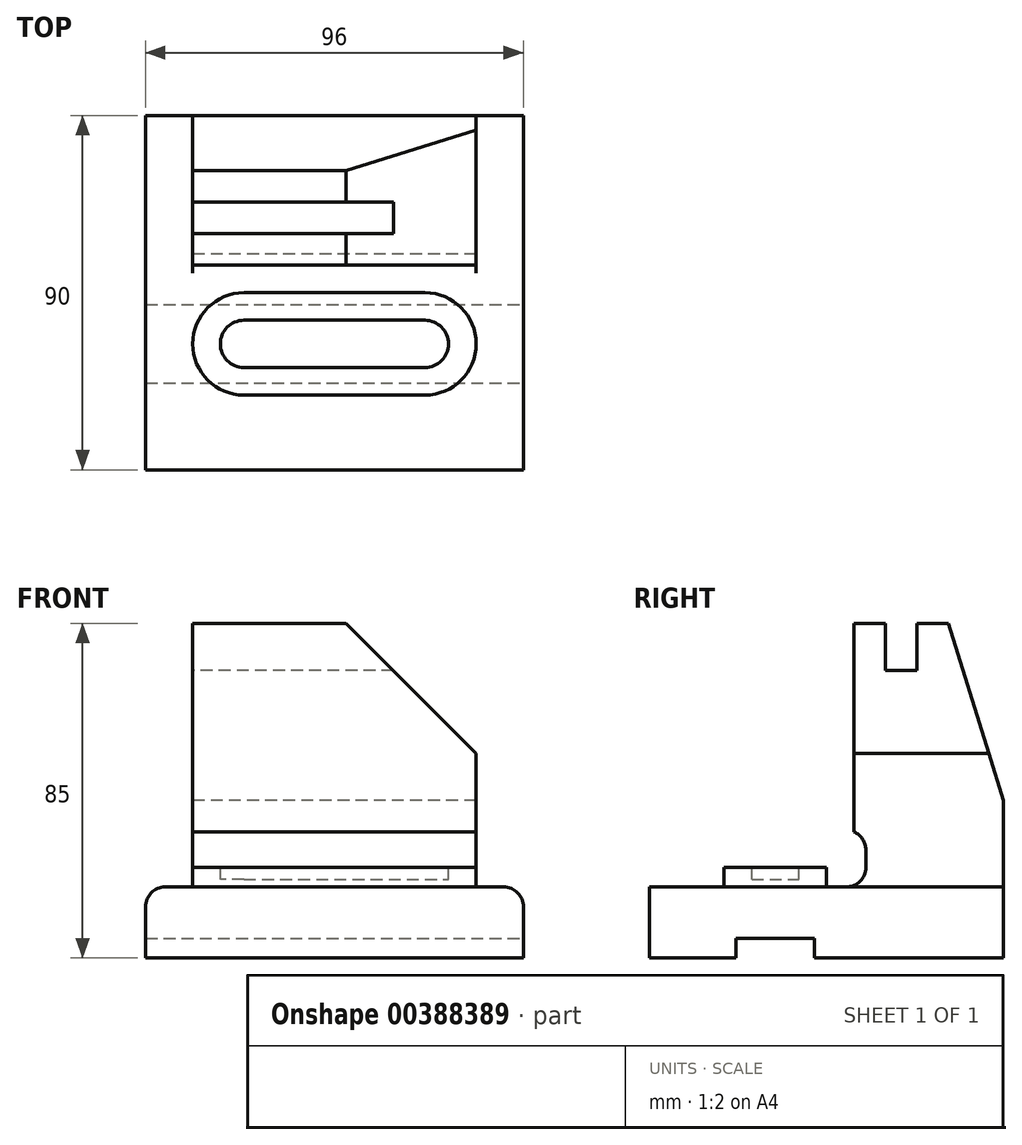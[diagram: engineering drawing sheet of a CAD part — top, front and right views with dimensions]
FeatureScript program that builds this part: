
annotation { "Feature Type Name" : "Feature", "Feature Type Description" : "" }
export const myFeature = defineFeature(function(context is Context, id is Id, definition is map)
    precondition{}
    {
        {
            var Q0;
            Q0=qCreatedBy(makeId("Top.planeOp"),FACE);
            var sketch = newSketch(context, id + "F0", { "sketchPlane" : qUnion([Q0])});
            skLineSegment(sketch, "E0.bottom", {"start": v(0, 0) * mm, "end": v(96, 0) * mm});
            skLineSegment(sketch, "E0.top", {"start": v(0, 90) * mm, "end": v(96, 90) * mm});
            skLineSegment(sketch, "E0.left", {"start": v(0, 0) * mm, "end": v(0, 90) * mm});
            skLineSegment(sketch, "E0.right", {"start": v(96, 0) * mm, "end": v(96, 90) * mm});
            skSolve(sketch);
        }
        {
            var Q0;
            Q0=makeQuery(id+"F0.imprint","IMPRINT",FACE,{"disambiguationData":[TD([[makeQuery(id+"F0.imprint","IMPRINT",EDGE,{"derivedFrom":sQuery(id+"F0.wireOp",EDGE,"E0.bottom")}),1.0]])]});
            extrude(context, id + "F1", {"entities" : qUnion([Q0]), "depth" : 18 * mm});
        }
        {
            var Q0;
            Q0=makeQuery(id+"F1.opExtrude","CAP_FACE",FACE,{"disambiguationData":[OSD([sQuery(id+"F0.wireOp",EDGE,"E0.bottom"),sQuery(id+"F0.wireOp",EDGE,"E0.top"),sQuery(id+"F0.wireOp",EDGE,"E0.left"),sQuery(id+"F0.wireOp",EDGE,"E0.right")])],"isStart":false});
            var sketch = newSketch(context, id + "F2", { "sketchPlane" : qUnion([Q0])});
            skLineSegment(sketch, "E1.bottom", {"start": v(12, 90) * mm, "end": v(84, 90) * mm});
            skLineSegment(sketch, "E1.top", {"start": v(12, 52) * mm, "end": v(84, 52) * mm});
            skLineSegment(sketch, "E1.left", {"start": v(12, 90) * mm, "end": v(12, 52) * mm});
            skLineSegment(sketch, "E1.right", {"start": v(84, 90) * mm, "end": v(84, 52) * mm});
            skSolve(sketch);
        }
        {
            var Q0;
            Q0=makeQuery(id+"F1.opExtrude","CAP_FACE",FACE,{"disambiguationData":[OSD([sQuery(id+"F0.wireOp",EDGE,"E0.bottom"),sQuery(id+"F0.wireOp",EDGE,"E0.top"),sQuery(id+"F0.wireOp",EDGE,"E0.left"),sQuery(id+"F0.wireOp",EDGE,"E0.right")])],"isStart":true});
            cPlane(context, id + "F3", {"entities" : qUnion([Q0]), "cplaneType" : CPlaneType.OFFSET, "offset" : 85 * mm, "oppositeDirection" : true, "width" : 150 * mm, "height" : 150 * mm});
        }
        {
            var Q0;
            Q0 = qSketchRegion(id + "F2", true);
            var Q1;
            Q1=qCreatedBy(id+"F3.planeOp",FACE);
            extrude(context, id + "F4", {"entities" : qUnion([Q0]), "operationType" : NewBodyOperationType.ADD, "endBound" : BoundingType.UP_TO_SURFACE, "endBoundEntityFace" : qUnion([Q1]), "depth" : 58 * mm});
        }
        {
            var Q0;
            Q0=makeQuery(id+"F4.opExtrude","SWEPT_FACE",FACE,{"disambiguationData":[OSD([sQuery(id+"F2.wireOp",EDGE,"E1.top")])]});
            var sketch = newSketch(context, id + "F5", { "sketchPlane" : qUnion([Q0])});
            skLineSegment(sketch, "E2", {"start": v(84, 85) * mm, "end": v(51, 85) * mm});
            skLineSegment(sketch, "E3", {"start": v(51, 85) * mm, "end": v(84, 52) * mm});
            skSolve(sketch);
        }
        {
            var Q0;
            {var subQ0=sQuery(id+"F5.wireOp",EDGE,"E2");Q0=makeQuery(id+"F5.imprint","IMPRINT",FACE,{"disambiguationData":[TD([[makeQuery(id+"F5.imprint","IMPRINT",EDGE,{"derivedFrom":subQ0}),1.0]])]});}
            extrude(context, id + "F6", {"entities" : qUnion([Q0]), "operationType" : NewBodyOperationType.REMOVE, "oppositeDirection" : true, "depth" : 38.4 * mm});
        }
        {
            var Q0;
            Q0=makeQuery(id+"F4.opExtrude","SWEPT_FACE",FACE,{"disambiguationData":[OSD([sQuery(id+"F2.wireOp",EDGE,"E1.left")])]});
            var sketch = newSketch(context, id + "F7", { "sketchPlane" : qUnion([Q0])});
            skLineSegment(sketch, "E4.bottom", {"start": v(-60, 85) * mm, "end": v(-68, 85) * mm});
            skLineSegment(sketch, "E4.top", {"start": v(-60, 73) * mm, "end": v(-68, 73) * mm});
            skLineSegment(sketch, "E4.left", {"start": v(-60, 85) * mm, "end": v(-60, 73) * mm});
            skLineSegment(sketch, "E4.right", {"start": v(-68, 85) * mm, "end": v(-68, 73) * mm});
            skSolve(sketch);
        }
        {
            var Q0;
            Q0=makeQuery(id+"F7.imprint","IMPRINT",FACE,{"disambiguationData":[TD([[makeQuery(id+"F7.imprint","IMPRINT",EDGE,{"derivedFrom":sQuery(id+"F7.wireOp",EDGE,"E4.bottom")}),1.0]])]});
            extrude(context, id + "F8", {"entities" : qUnion([Q0]), "operationType" : NewBodyOperationType.REMOVE, "oppositeDirection" : true, "depth" : 71 * mm});
        }
        {
            var Q0;
            Q0=makeQuery(id+"F4.opExtrude","SWEPT_FACE",FACE,{"disambiguationData":[OSD([sQuery(id+"F2.wireOp",EDGE,"E1.left")])]});
            var sketch = newSketch(context, id + "F9", { "sketchPlane" : qUnion([Q0])});
            skLineSegment(sketch, "E5", {"start": v(-76, 85) * mm, "end": v(-90, 40) * mm});
            skSolve(sketch);
        }
        {
            var Q0;
            Q0 = qSketchRegion(id + "F9", true);
            var Q1;
            {var subQ0=sQuery(id+"F9.wireOp",EDGE,"E5");Q1=makeQuery(id+"F9.imprint","IMPRINT",FACE,{"disambiguationData":[TD([[makeQuery(id+"F9.imprint","IMPRINT",EDGE,{"derivedFrom":subQ0}),-1.0]])]});}
            extrude(context, id + "F10", {"entities" : qUnion([Q0, Q1]), "operationType" : NewBodyOperationType.REMOVE, "oppositeDirection" : true, "depth" : 143.3 * mm});
        }
        {
            var Q0;
            Q0=makeQuery(id+"F1.opExtrude","SWEPT_FACE",FACE,{"disambiguationData":[OSD([sQuery(id+"F0.wireOp",EDGE,"E0.right")])]});
            var sketch = newSketch(context, id + "F11", { "sketchPlane" : qUnion([Q0])});
            skLineSegment(sketch, "E6.bottom", {"start": v(22, 0) * mm, "end": v(42, 0) * mm});
            skLineSegment(sketch, "E6.top", {"start": v(22, 5) * mm, "end": v(42, 5) * mm});
            skLineSegment(sketch, "E6.left", {"start": v(22, 0) * mm, "end": v(22, 5) * mm});
            skLineSegment(sketch, "E6.right", {"start": v(42, 0) * mm, "end": v(42, 5) * mm});
            skPoint(sketch, "E7", {"position": v(32, 5) * mm});
            skSolve(sketch);
        }
        {
            var Q0;
            Q0=makeQuery(id+"F11.imprint","IMPRINT",FACE,{"disambiguationData":[TD([[makeQuery(id+"F11.imprint","IMPRINT",EDGE,{"derivedFrom":sQuery(id+"F11.wireOp",EDGE,"E6.bottom")}),1.0]])]});
            extrude(context, id + "F12", {"entities" : qUnion([Q0]), "operationType" : NewBodyOperationType.REMOVE, "oppositeDirection" : true, "depth" : 107.3 * mm});
        }
        {
            var Q0;
            Q0=makeQuery(id+"F1.opExtrude","CAP_FACE",FACE,{"disambiguationData":[OSD([sQuery(id+"F0.wireOp",EDGE,"E0.bottom"),sQuery(id+"F0.wireOp",EDGE,"E0.top"),sQuery(id+"F0.wireOp",EDGE,"E0.left"),sQuery(id+"F0.wireOp",EDGE,"E0.right")])],"isStart":false});
            var sketch = newSketch(context, id + "F13", { "sketchPlane" : qUnion([Q0])});
            skLineSegment(sketch, "E8.bottom", {"start": v(25, 45) * mm, "end": v(71, 45) * mm});
            skLineSegment(sketch, "E8.top", {"start": v(25, 19) * mm, "end": v(71, 19) * mm});
            skLineSegment(sketch, "E8.left", {"start": v(25, 45) * mm, "end": v(25, 19) * mm});
            skLineSegment(sketch, "E8.right", {"start": v(71, 45) * mm, "end": v(71, 19) * mm});
            skLineSegment(sketch, "E9", {"start": v(25, 32) * mm, "end": v(71, 32) * mm, "construction": true});
            skArc(sketch, "E10", {"start": v(25, 45) * mm, "mid": v(12, 32) * mm, "end": v(25, 19) * mm});
            skArc(sketch, "E11", {"start": v(71, 19) * mm, "mid": v(84, 32) * mm, "end": v(71, 45) * mm});
            skSolve(sketch);
        }
        {
            var Q0;
            Q0=makeQuery(id+"F13.imprint","IMPRINT",FACE,{"disambiguationData":[TD([[makeQuery(id+"F13.imprint","IMPRINT",EDGE,{"derivedFrom":sQuery(id+"F13.wireOp",EDGE,"E8.left")}),-1.0]])]});
            var Q1;
            Q1=makeQuery(id+"F13.imprint","IMPRINT",FACE,{"disambiguationData":[TD([[makeQuery(id+"F13.imprint","IMPRINT",EDGE,{"derivedFrom":sQuery(id+"F13.wireOp",EDGE,"E8.right")}),1.0]])]});
            var Q2;
            Q2=makeQuery(id+"F13.imprint","IMPRINT",FACE,{"disambiguationData":[TD([[makeQuery(id+"F13.imprint","IMPRINT",EDGE,{"derivedFrom":sQuery(id+"F13.wireOp",EDGE,"E8.bottom")}),-1.0]])]});
            extrude(context, id + "F14", {"entities" : qUnion([Q0, Q1, Q2]), "operationType" : NewBodyOperationType.ADD, "depth" : 5 * mm});
        }
        {
            var Q0;
            Q0=makeQuery(id+"F14.opExtrude","CAP_FACE",FACE,{"disambiguationData":[OSD([sQuery(id+"F13.wireOp",EDGE,"E8.bottom"),sQuery(id+"F13.wireOp",EDGE,"E8.top"),sQuery(id+"F13.wireOp",EDGE,"E10"),sQuery(id+"F13.wireOp",EDGE,"E11")])],"isStart":false});
            var sketch = newSketch(context, id + "F15", { "sketchPlane" : qUnion([Q0])});
            skLineSegment(sketch, "E12.bottom", {"start": v(25, 38) * mm, "end": v(71, 38) * mm});
            skLineSegment(sketch, "E12.top", {"start": v(25, 26) * mm, "end": v(71, 26) * mm});
            skLineSegment(sketch, "E12.left", {"start": v(25, 38) * mm, "end": v(25, 26) * mm});
            skLineSegment(sketch, "E12.right", {"start": v(71, 38) * mm, "end": v(71, 26) * mm});
            skArc(sketch, "E13", {"start": v(71, 26) * mm, "mid": v(77, 32) * mm, "end": v(71, 38) * mm});
            skArc(sketch, "E14", {"start": v(25, 38) * mm, "mid": v(19, 32) * mm, "end": v(25, 26) * mm});
            skSolve(sketch);
        }
        {
            var Q0;
            Q0=makeQuery(id+"F15.imprint","IMPRINT",FACE,{"disambiguationData":[TD([[makeQuery(id+"F15.imprint","IMPRINT",EDGE,{"derivedFrom":sQuery(id+"F15.wireOp",EDGE,"E12.bottom")}),-1.0]])]});
            var Q1;
            Q1=makeQuery(id+"F15.imprint","IMPRINT",FACE,{"disambiguationData":[TD([[makeQuery(id+"F15.imprint","IMPRINT",EDGE,{"derivedFrom":sQuery(id+"F15.wireOp",EDGE,"E12.right")}),1.0]])]});
            var Q2;
            Q2=makeQuery(id+"F15.imprint","IMPRINT",FACE,{"disambiguationData":[TD([[makeQuery(id+"F15.imprint","IMPRINT",EDGE,{"derivedFrom":sQuery(id+"F15.wireOp",EDGE,"E12.left")}),-1.0]])]});
            extrude(context, id + "F16", {"entities" : qUnion([Q0, Q1, Q2]), "operationType" : NewBodyOperationType.REMOVE, "oppositeDirection" : true, "depth" : 3 * mm});
        }
        {
            var Q0;
            Q0=makeQuery(id+"F4.opExtrude","SWEPT_FACE",FACE,{"disambiguationData":[OSD([sQuery(id+"F2.wireOp",EDGE,"E1.right")])]});
            var sketch = newSketch(context, id + "F17", { "sketchPlane" : qUnion([Q0])});
            skLineSegment(sketch, "E15.bottom", {"start": v(52, 18) * mm, "end": v(55, 18) * mm});
            skLineSegment(sketch, "E15.top", {"start": v(52, 32) * mm, "end": v(55, 32) * mm});
            skLineSegment(sketch, "E15.left", {"start": v(52, 18) * mm, "end": v(52, 32) * mm});
            skLineSegment(sketch, "E15.right", {"start": v(55, 18) * mm, "end": v(55, 32) * mm});
            skSolve(sketch);
        }
        {
            var Q0;
            Q0 = qSketchRegion(id + "F17", true);
            extrude(context, id + "F18", {"entities" : qUnion([Q0]), "operationType" : NewBodyOperationType.REMOVE, "oppositeDirection" : true, "depth" : 78.3 * mm});
        }
        {
            var Q0;
            Q0=makeQuery(id+"F18.boolean.opBoolean","COPY",EDGE,{"derivedFrom":makeQuery(id+"F18.opExtrude","SWEPT_EDGE",EDGE,{"disambiguationData":[OSD([sQuery(id+"F2.wireOp",EDGE,"E1.right"),sQuery(id+"F17.wireOp",EDGE,"E15.bottom"),sQuery(id+"F17.wireOp",EDGE,"E15.right")])]})});
            var Q1;
            Q1=makeQuery(id+"F18.boolean.opBoolean","COPY",EDGE,{"derivedFrom":makeQuery(id+"F18.opExtrude","SWEPT_EDGE",EDGE,{"disambiguationData":[OSD([sQuery(id+"F17.wireOp",EDGE,"E15.top"),sQuery(id+"F17.wireOp",EDGE,"E15.right")])]})});
            var Q2;
            Q2=makeQuery(id+"F1.opExtrude","CAP_EDGE",EDGE,{"disambiguationData":[OSD([sQuery(id+"F0.wireOp",EDGE,"E0.right")])],"isStart":false});
            var Q3;
            Q3=makeQuery(id+"F1.opExtrude","CAP_EDGE",EDGE,{"disambiguationData":[OSD([sQuery(id+"F0.wireOp",EDGE,"E0.left")])],"isStart":false});
            var Q4;
            Q4=makeQuery(id+"F4.opExtrude","CAP_EDGE",EDGE,{"disambiguationData":[OSD([sQuery(id+"F2.wireOp",EDGE,"E1.right")])],"isStart":true});
            var Q5;
            Q5=makeQuery(id+"F4.opExtrude","CAP_EDGE",EDGE,{"disambiguationData":[OSD([sQuery(id+"F2.wireOp",EDGE,"E1.left")])],"isStart":true});
            var Q6;
            Q6=makeQuery(id+"F14.opExtrude","CAP_EDGE",EDGE,{"disambiguationData":[OSD([sQuery(id+"F13.wireOp",EDGE,"E8.top")])],"isStart":true});
            fillet(context, id + "F19", {"entities" : qUnion([Q0, Q1, Q2, Q3, Q4, Q5, Q6]), "radius" : 5 * mm, "tangentPropagation" : true, "allowEdgeOverflow" : false});
        }
    });
